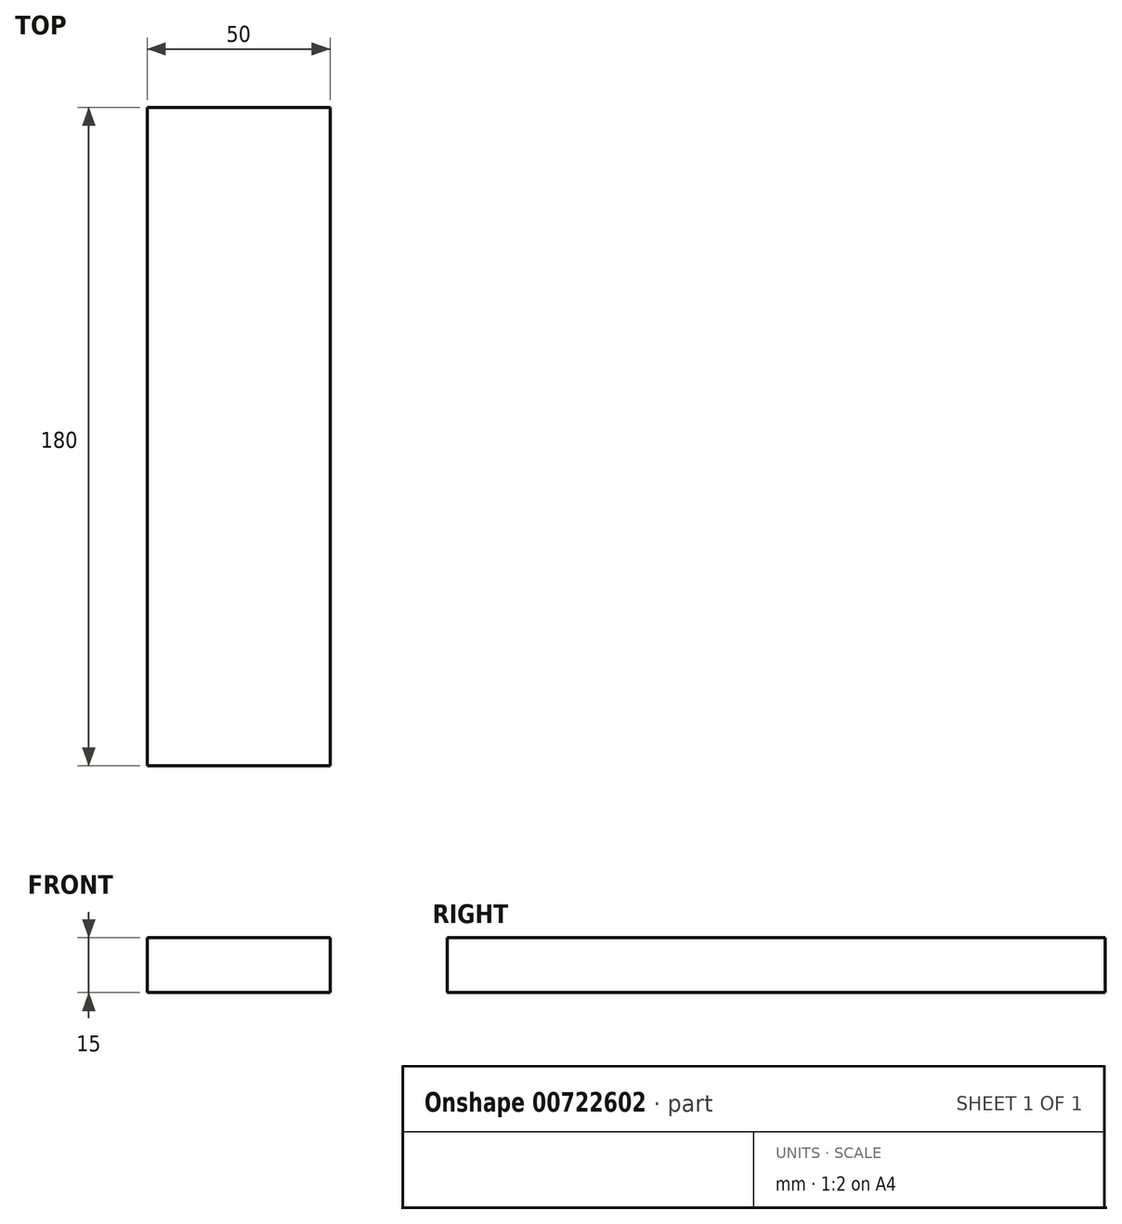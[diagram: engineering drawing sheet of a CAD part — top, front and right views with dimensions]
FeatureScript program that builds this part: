
annotation { "Feature Type Name" : "Feature", "Feature Type Description" : "" }
export const myFeature = defineFeature(function(context is Context, id is Id, definition is map)
    precondition{}
    {
        {
            var Q0;
            Q0=qCreatedBy(makeId("Front.planeOp"),FACE);
            var sketch = newSketch(context, id + "F0", { "sketchPlane" : qUnion([Q0])});
            skLineSegment(sketch, "E0.bottom", {"start": v(-25, -7.5) * mm, "end": v(25, -7.5) * mm});
            skLineSegment(sketch, "E0.top", {"start": v(-25, 7.5) * mm, "end": v(25, 7.5) * mm});
            skLineSegment(sketch, "E0.left", {"start": v(-25, -7.5) * mm, "end": v(-25, 7.5) * mm});
            skLineSegment(sketch, "E0.right", {"start": v(25, -7.5) * mm, "end": v(25, 7.5) * mm});
            skPoint(sketch, "E0.middle", {"position": v(0, 0) * mm});
            skSolve(sketch);
        }
        {
            var Q0;
            Q0=makeQuery(id+"F0.imprint","IMPRINT",FACE,{"disambiguationData":[TD([[makeQuery(id+"F0.imprint","IMPRINT",EDGE,{"derivedFrom":sQuery(id+"F0.wireOp",EDGE,"E0.bottom")}),1.0]])]});
            extrude(context, id + "F1", {"entities" : qUnion([Q0]), "endBound" : BoundingType.SYMMETRIC, "depth" : 180 * mm, "offsetDistance" : 25 * mm});
        }
    });
